# Revit family: 6v
name_source: partatom
category: Pipe Accessories
revit_build: Autodesk Revit 2018 (Build: 20170223_1515(x64)
units: mm (PartAtom-declared; Revit-internal decimal feet)

## family parameters
Cut with Voids When Loaded = No
Host = Face
OmniClass Number = 23.27.43.00
OmniClass Title = Pipe Fittings
Part Type = Normal
Round Connector Dimension = Use Diameter
Shared = No

## types (3) — shared parameters
Assembly Code = D2040100
BIMobject category = Joints
Default Elevation = 1219 mm
Description = Flat Gasket For Flange
Design country = Italy
Edition number = 1
IFC Classification = Pipe Fitting
Keynote = 15410
Manufacturer = Aignep Spa
Manufacturer country = Italy
Manufacturer name = Aignep Spa
Material main = Polymer
Model = 90017
OmniClass Code = 23-27 43 00
OmniClass Description = Pipe Fittings
Product Guid = 4de537a5-125b-4fcd-8996-acf08573e598
Product Material = AIGNEP - Rubber - Black
Product SKU = Flat-Gasket-For-Flange-90017
Product certification = https://www.aignep.com
Product data url = https://www.bimobject.com
Product family = INFINITY
Product group = Seals
Product name = Flat Gasket For Flange - 90017
Product url = https://www.aignep.com
QR code = https://www.bimobject.com
S = 2 mm  [stored 0.00656168 ft]
URL = https://www.aignep.com

## per-type parameters (varying)
| type | D1 | D2 | Tick Size |
| 90017 00 57 TP 00 | 115 mm  [stored 0.377297 ft] | 162 mm  [stored 0.531496 ft] | 44 mm |
| 90017 00 57 HT 00 | 89 mm  [stored 0.291995 ft] | 131 mm  [stored 0.42979 ft] | 32 mm  [stored 0.104987 ft] |
| 90017 00 57 ZW 00 | 169 mm  [stored 0.554462 ft] | 220 mm  [stored 0.721785 ft] | 67 mm |

note: [stored X ft] marks values corroborated as IEEE doubles in the binary element streams (Revit-internal decimal feet)

## geometry (parser evidence)
native form markers: Sweep x2
no freeform markers — native parametric forms only
